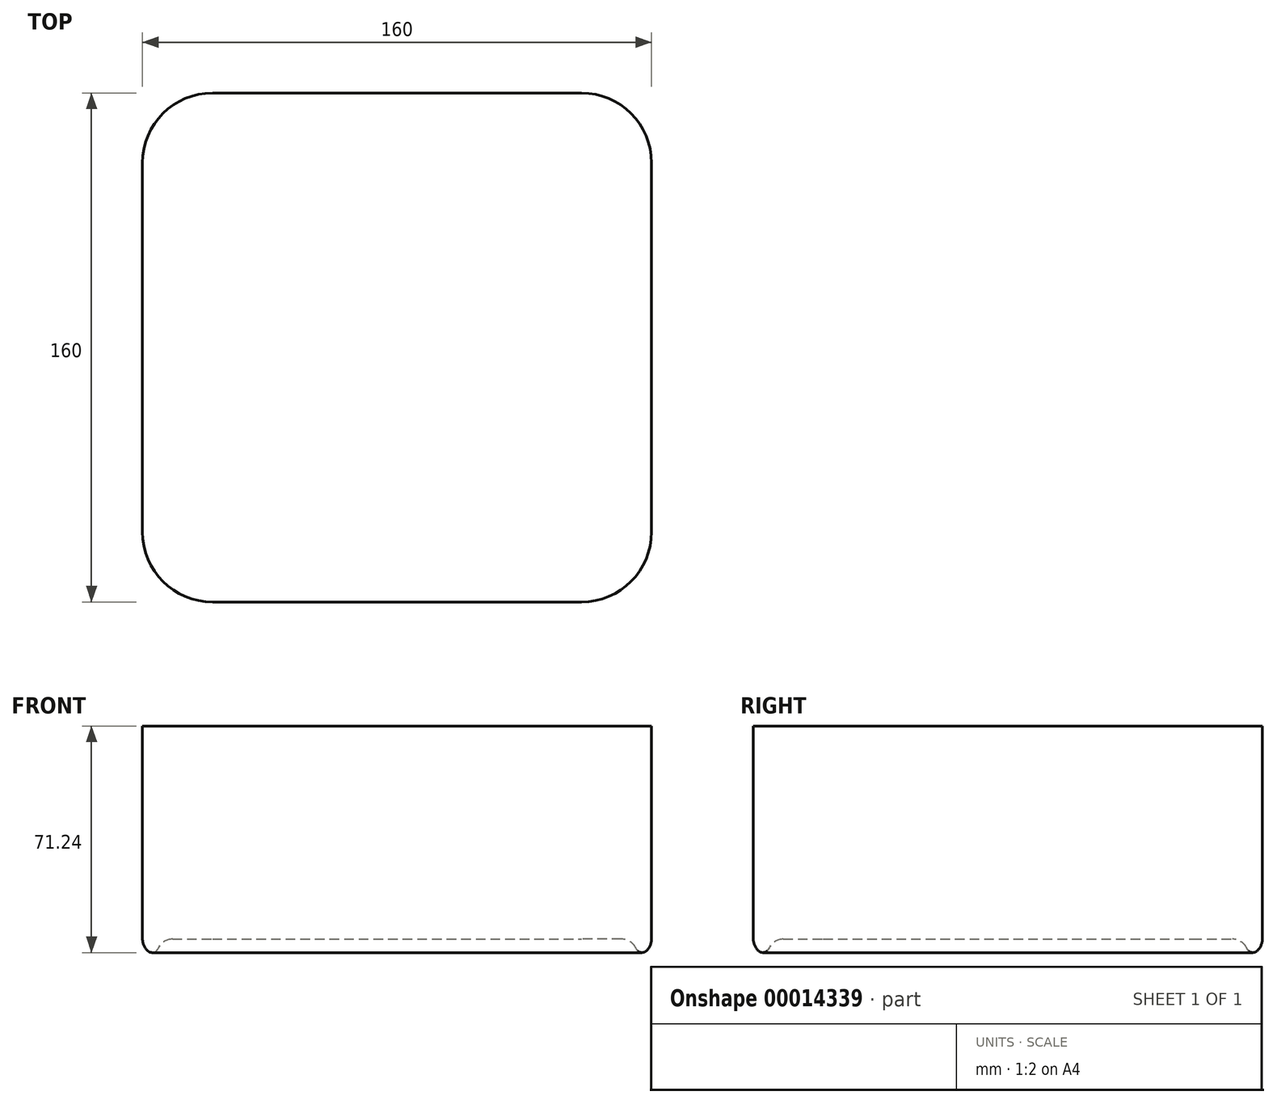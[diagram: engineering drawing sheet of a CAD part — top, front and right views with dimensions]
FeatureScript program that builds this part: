
annotation { "Feature Type Name" : "Feature", "Feature Type Description" : "" }
export const myFeature = defineFeature(function(context is Context, id is Id, definition is map)
    precondition{}
    {
        {
            var Q0;
            Q0=qCreatedBy(makeId("Top.planeOp"),FACE);
            var sketch = newSketch(context, id + "F0", { "sketchPlane" : qUnion([Q0])});
            skLineSegment(sketch, "E0.rect.bottom", {"start": v(80, -80) * mm, "end": v(-80, -80) * mm});
            skLineSegment(sketch, "E0.rect.top", {"start": v(80, 80) * mm, "end": v(-80, 80) * mm});
            skLineSegment(sketch, "E0.rect.left", {"start": v(80, -80) * mm, "end": v(80, 80) * mm});
            skLineSegment(sketch, "E0.rect.right", {"start": v(-80, -80) * mm, "end": v(-80, 80) * mm});
            skPoint(sketch, "E0.rect.middle", {"position": v(0, 0) * mm});
            skSolve(sketch);
        }
        {
            var Q0;
            Q0=makeQuery(id+"F0.imprint","IMPRINT",FACE,{"disambiguationData":[TD([[makeQuery(id+"F0.imprint","IMPRINT",EDGE,{"derivedFrom":sQuery(id+"F0.wireOp",EDGE,"E0.rect.bottom")}),-1.0]])]});
            extrude(context, id + "F1", {"entities" : qUnion([Q0]), "depth" : 72 * mm});
        }
        {
            var Q0;
            Q0=makeQuery(id+"F1.opExtrude","SWEPT_EDGE",EDGE,{"disambiguationData":[OSD([sQuery(id+"F0.wireOp",EDGE,"E0.rect.bottom"),sQuery(id+"F0.wireOp",EDGE,"E0.rect.right")])]});
            var Q1;
            Q1=makeQuery(id+"F1.opExtrude","SWEPT_EDGE",EDGE,{"disambiguationData":[OSD([sQuery(id+"F0.wireOp",EDGE,"E0.rect.bottom"),sQuery(id+"F0.wireOp",EDGE,"E0.rect.left")])]});
            var Q2;
            Q2=makeQuery(id+"F1.opExtrude","SWEPT_EDGE",EDGE,{"disambiguationData":[OSD([sQuery(id+"F0.wireOp",EDGE,"E0.rect.top"),sQuery(id+"F0.wireOp",EDGE,"E0.rect.left")])]});
            var Q3;
            Q3=makeQuery(id+"F1.opExtrude","SWEPT_EDGE",EDGE,{"disambiguationData":[OSD([sQuery(id+"F0.wireOp",EDGE,"E0.rect.top"),sQuery(id+"F0.wireOp",EDGE,"E0.rect.right")])]});
            fillet(context, id + "F2", {"entities" : qUnion([Q0, Q1, Q2, Q3]), "radius" : 22 * mm, "tangentPropagation" : true, "allowEdgeOverflow" : false});
        }
        {
            var Q0;
            Q0=makeQuery(id+"F1.opExtrude","CAP_FACE",FACE,{"disambiguationData":[OSD([sQuery(id+"F0.wireOp",EDGE,"E0.rect.bottom"),sQuery(id+"F0.wireOp",EDGE,"E0.rect.top"),sQuery(id+"F0.wireOp",EDGE,"E0.rect.left"),sQuery(id+"F0.wireOp",EDGE,"E0.rect.right")])],"isStart":true});
            fillet(context, id + "F3", {"entities" : qUnion([Q0]), "radius" : 5 * mm, "tangentPropagation" : true, "allowEdgeOverflow" : false});
        }
        {
            var Q0;
            Q0=makeQuery(id+"F1.opExtrude","CAP_FACE",FACE,{"disambiguationData":[OSD([sQuery(id+"F0.wireOp",EDGE,"E0.rect.bottom"),sQuery(id+"F0.wireOp",EDGE,"E0.rect.top"),sQuery(id+"F0.wireOp",EDGE,"E0.rect.left"),sQuery(id+"F0.wireOp",EDGE,"E0.rect.right")])],"isStart":true});
            extrude(context, id + "F4", {"entities" : qUnion([Q0]), "operationType" : NewBodyOperationType.REMOVE, "oppositeDirection" : true, "depth" : 5 * mm});
        }
        {
            var Q0;
            {var subQ0=sQuery(id+"F0.wireOp",EDGE,"E0.rect.top");var subQ1=sQuery(id+"F0.wireOp",EDGE,"E0.rect.right");var subQ2=sQuery(id+"F0.wireOp",EDGE,"E0.rect.bottom");var subQ3=sQuery(id+"F0.wireOp",EDGE,"E0.rect.left");var subQ4=makeQuery(id+"F1.opExtrude","CAP_FACE",FACE,{"disambiguationData":[OSD([subQ2,subQ0,subQ3,subQ1])],"isStart":true});var subQ5=makeQuery(id+"F3.opFillet","BLEND_EDGE",EDGE,{"blendedFrom":[makeQuery(id+"F2.opFillet","BLEND_EDGE",EDGE,{"blendedFrom":[makeQuery(id+"F1.opExtrude","SWEPT_EDGE",EDGE,{"disambiguationData":[OSD([subQ0,subQ1])]}),subQ4],"blendedInto":[subQ4]}),subQ4],"blendedInto":[subQ4]});Q0=makeQuery(id+"F4.boolean.opBoolean","MERGE",EDGE,{"derivedFrom":[subQ5,makeQuery(id+"F4.opExtrude","CAP_EDGE",EDGE,{"disambiguationData":[OSD([subQ2,subQ0,subQ3,subQ1]),TDD([subQ5])],"isStart":true})]});}
            var Q1;
            {var subQ0=sQuery(id+"F0.wireOp",EDGE,"E0.rect.top");var subQ1=sQuery(id+"F0.wireOp",EDGE,"E0.rect.bottom");var subQ2=sQuery(id+"F0.wireOp",EDGE,"E0.rect.left");var subQ3=sQuery(id+"F0.wireOp",EDGE,"E0.rect.right");var subQ4=makeQuery(id+"F3.opFillet","BLEND_EDGE",EDGE,{"blendedFrom":[makeQuery(id+"F1.opExtrude","CAP_EDGE",EDGE,{"disambiguationData":[OSD([subQ0])],"isStart":true}),makeQuery(id+"F1.opExtrude","CAP_FACE",FACE,{"disambiguationData":[OSD([subQ1,subQ0,subQ2,subQ3])],"isStart":true})],"blendedInto":[makeQuery(id+"F1.opExtrude","CAP_FACE",FACE,{"disambiguationData":[OSD([subQ1,subQ0,subQ2,subQ3])],"isStart":true})]});Q1=makeQuery(id+"F4.boolean.opBoolean","MERGE",EDGE,{"derivedFrom":[subQ4,makeQuery(id+"F4.opExtrude","CAP_EDGE",EDGE,{"disambiguationData":[OSD([subQ1,subQ0,subQ2,subQ3]),TDD([subQ4])],"isStart":true})]});}
            var Q2;
            {var subQ0=sQuery(id+"F0.wireOp",EDGE,"E0.rect.right");var subQ1=sQuery(id+"F0.wireOp",EDGE,"E0.rect.bottom");var subQ2=sQuery(id+"F0.wireOp",EDGE,"E0.rect.top");var subQ3=sQuery(id+"F0.wireOp",EDGE,"E0.rect.left");var subQ4=makeQuery(id+"F3.opFillet","BLEND_EDGE",EDGE,{"blendedFrom":[makeQuery(id+"F1.opExtrude","CAP_EDGE",EDGE,{"disambiguationData":[OSD([subQ0])],"isStart":true}),makeQuery(id+"F1.opExtrude","CAP_FACE",FACE,{"disambiguationData":[OSD([subQ1,subQ2,subQ3,subQ0])],"isStart":true})],"blendedInto":[makeQuery(id+"F1.opExtrude","CAP_FACE",FACE,{"disambiguationData":[OSD([subQ1,subQ2,subQ3,subQ0])],"isStart":true})]});Q2=makeQuery(id+"F4.boolean.opBoolean","MERGE",EDGE,{"derivedFrom":[subQ4,makeQuery(id+"F4.opExtrude","CAP_EDGE",EDGE,{"disambiguationData":[OSD([subQ1,subQ2,subQ3,subQ0]),TDD([subQ4])],"isStart":true})]});}
            var Q3;
            {var subQ0=sQuery(id+"F0.wireOp",EDGE,"E0.rect.bottom");var subQ1=sQuery(id+"F0.wireOp",EDGE,"E0.rect.right");var subQ2=sQuery(id+"F0.wireOp",EDGE,"E0.rect.top");var subQ3=sQuery(id+"F0.wireOp",EDGE,"E0.rect.left");var subQ4=makeQuery(id+"F1.opExtrude","CAP_FACE",FACE,{"disambiguationData":[OSD([subQ0,subQ2,subQ3,subQ1])],"isStart":true});var subQ5=makeQuery(id+"F3.opFillet","BLEND_EDGE",EDGE,{"blendedFrom":[makeQuery(id+"F2.opFillet","BLEND_EDGE",EDGE,{"blendedFrom":[makeQuery(id+"F1.opExtrude","SWEPT_EDGE",EDGE,{"disambiguationData":[OSD([subQ0,subQ1])]}),subQ4],"blendedInto":[subQ4]}),subQ4],"blendedInto":[subQ4]});Q3=makeQuery(id+"F4.boolean.opBoolean","MERGE",EDGE,{"derivedFrom":[subQ5,makeQuery(id+"F4.opExtrude","CAP_EDGE",EDGE,{"disambiguationData":[OSD([subQ0,subQ2,subQ3,subQ1]),TDD([subQ5])],"isStart":true})]});}
            var Q4;
            {var subQ0=sQuery(id+"F0.wireOp",EDGE,"E0.rect.bottom");var subQ1=sQuery(id+"F0.wireOp",EDGE,"E0.rect.top");var subQ2=sQuery(id+"F0.wireOp",EDGE,"E0.rect.left");var subQ3=sQuery(id+"F0.wireOp",EDGE,"E0.rect.right");var subQ4=makeQuery(id+"F3.opFillet","BLEND_EDGE",EDGE,{"blendedFrom":[makeQuery(id+"F1.opExtrude","CAP_EDGE",EDGE,{"disambiguationData":[OSD([subQ0])],"isStart":true}),makeQuery(id+"F1.opExtrude","CAP_FACE",FACE,{"disambiguationData":[OSD([subQ0,subQ1,subQ2,subQ3])],"isStart":true})],"blendedInto":[makeQuery(id+"F1.opExtrude","CAP_FACE",FACE,{"disambiguationData":[OSD([subQ0,subQ1,subQ2,subQ3])],"isStart":true})]});Q4=makeQuery(id+"F4.boolean.opBoolean","MERGE",EDGE,{"derivedFrom":[subQ4,makeQuery(id+"F4.opExtrude","CAP_EDGE",EDGE,{"disambiguationData":[OSD([subQ0,subQ1,subQ2,subQ3]),TDD([subQ4])],"isStart":true})]});}
            var Q5;
            {var subQ0=sQuery(id+"F0.wireOp",EDGE,"E0.rect.bottom");var subQ1=sQuery(id+"F0.wireOp",EDGE,"E0.rect.left");var subQ2=sQuery(id+"F0.wireOp",EDGE,"E0.rect.top");var subQ3=sQuery(id+"F0.wireOp",EDGE,"E0.rect.right");var subQ4=makeQuery(id+"F1.opExtrude","CAP_FACE",FACE,{"disambiguationData":[OSD([subQ0,subQ2,subQ1,subQ3])],"isStart":true});var subQ5=makeQuery(id+"F3.opFillet","BLEND_EDGE",EDGE,{"blendedFrom":[makeQuery(id+"F2.opFillet","BLEND_EDGE",EDGE,{"blendedFrom":[makeQuery(id+"F1.opExtrude","SWEPT_EDGE",EDGE,{"disambiguationData":[OSD([subQ0,subQ1])]}),subQ4],"blendedInto":[subQ4]}),subQ4],"blendedInto":[subQ4]});Q5=makeQuery(id+"F4.boolean.opBoolean","MERGE",EDGE,{"derivedFrom":[subQ5,makeQuery(id+"F4.opExtrude","CAP_EDGE",EDGE,{"disambiguationData":[OSD([subQ0,subQ2,subQ1,subQ3]),TDD([subQ5])],"isStart":true})]});}
            var Q6;
            {var subQ0=sQuery(id+"F0.wireOp",EDGE,"E0.rect.left");var subQ1=sQuery(id+"F0.wireOp",EDGE,"E0.rect.bottom");var subQ2=sQuery(id+"F0.wireOp",EDGE,"E0.rect.top");var subQ3=sQuery(id+"F0.wireOp",EDGE,"E0.rect.right");var subQ4=makeQuery(id+"F3.opFillet","BLEND_EDGE",EDGE,{"blendedFrom":[makeQuery(id+"F1.opExtrude","CAP_EDGE",EDGE,{"disambiguationData":[OSD([subQ0])],"isStart":true}),makeQuery(id+"F1.opExtrude","CAP_FACE",FACE,{"disambiguationData":[OSD([subQ1,subQ2,subQ0,subQ3])],"isStart":true})],"blendedInto":[makeQuery(id+"F1.opExtrude","CAP_FACE",FACE,{"disambiguationData":[OSD([subQ1,subQ2,subQ0,subQ3])],"isStart":true})]});Q6=makeQuery(id+"F4.boolean.opBoolean","MERGE",EDGE,{"derivedFrom":[subQ4,makeQuery(id+"F4.opExtrude","CAP_EDGE",EDGE,{"disambiguationData":[OSD([subQ1,subQ2,subQ0,subQ3]),TDD([subQ4])],"isStart":true})]});}
            var Q7;
            {var subQ0=sQuery(id+"F0.wireOp",EDGE,"E0.rect.top");var subQ1=sQuery(id+"F0.wireOp",EDGE,"E0.rect.left");var subQ2=sQuery(id+"F0.wireOp",EDGE,"E0.rect.bottom");var subQ3=sQuery(id+"F0.wireOp",EDGE,"E0.rect.right");var subQ4=makeQuery(id+"F1.opExtrude","CAP_FACE",FACE,{"disambiguationData":[OSD([subQ2,subQ0,subQ1,subQ3])],"isStart":true});var subQ5=makeQuery(id+"F3.opFillet","BLEND_EDGE",EDGE,{"blendedFrom":[makeQuery(id+"F2.opFillet","BLEND_EDGE",EDGE,{"blendedFrom":[makeQuery(id+"F1.opExtrude","SWEPT_EDGE",EDGE,{"disambiguationData":[OSD([subQ0,subQ1])]}),subQ4],"blendedInto":[subQ4]}),subQ4],"blendedInto":[subQ4]});Q7=makeQuery(id+"F4.boolean.opBoolean","MERGE",EDGE,{"derivedFrom":[subQ5,makeQuery(id+"F4.opExtrude","CAP_EDGE",EDGE,{"disambiguationData":[OSD([subQ2,subQ0,subQ1,subQ3]),TDD([subQ5])],"isStart":true})]});}
            fillet(context, id + "F5", {"entities" : qUnion([Q0, Q1, Q2, Q3, Q4, Q5, Q6, Q7]), "radius" : 2 * mm, "tangentPropagation" : true, "allowEdgeOverflow" : false});
        }
        {
            var Q0;
            Q0=makeQuery(id+"F4.boolean.opBoolean","COPY",FACE,{"derivedFrom":makeQuery(id+"F4.opExtrude","CAP_FACE",FACE,{"disambiguationData":[OSD([sQuery(id+"F0.wireOp",EDGE,"E0.rect.bottom"),sQuery(id+"F0.wireOp",EDGE,"E0.rect.top"),sQuery(id+"F0.wireOp",EDGE,"E0.rect.left"),sQuery(id+"F0.wireOp",EDGE,"E0.rect.right")])],"isStart":false})});
            fillet(context, id + "F6", {"entities" : qUnion([Q0]), "radius" : 5 * mm, "tangentPropagation" : true, "allowEdgeOverflow" : false});
        }
    });
